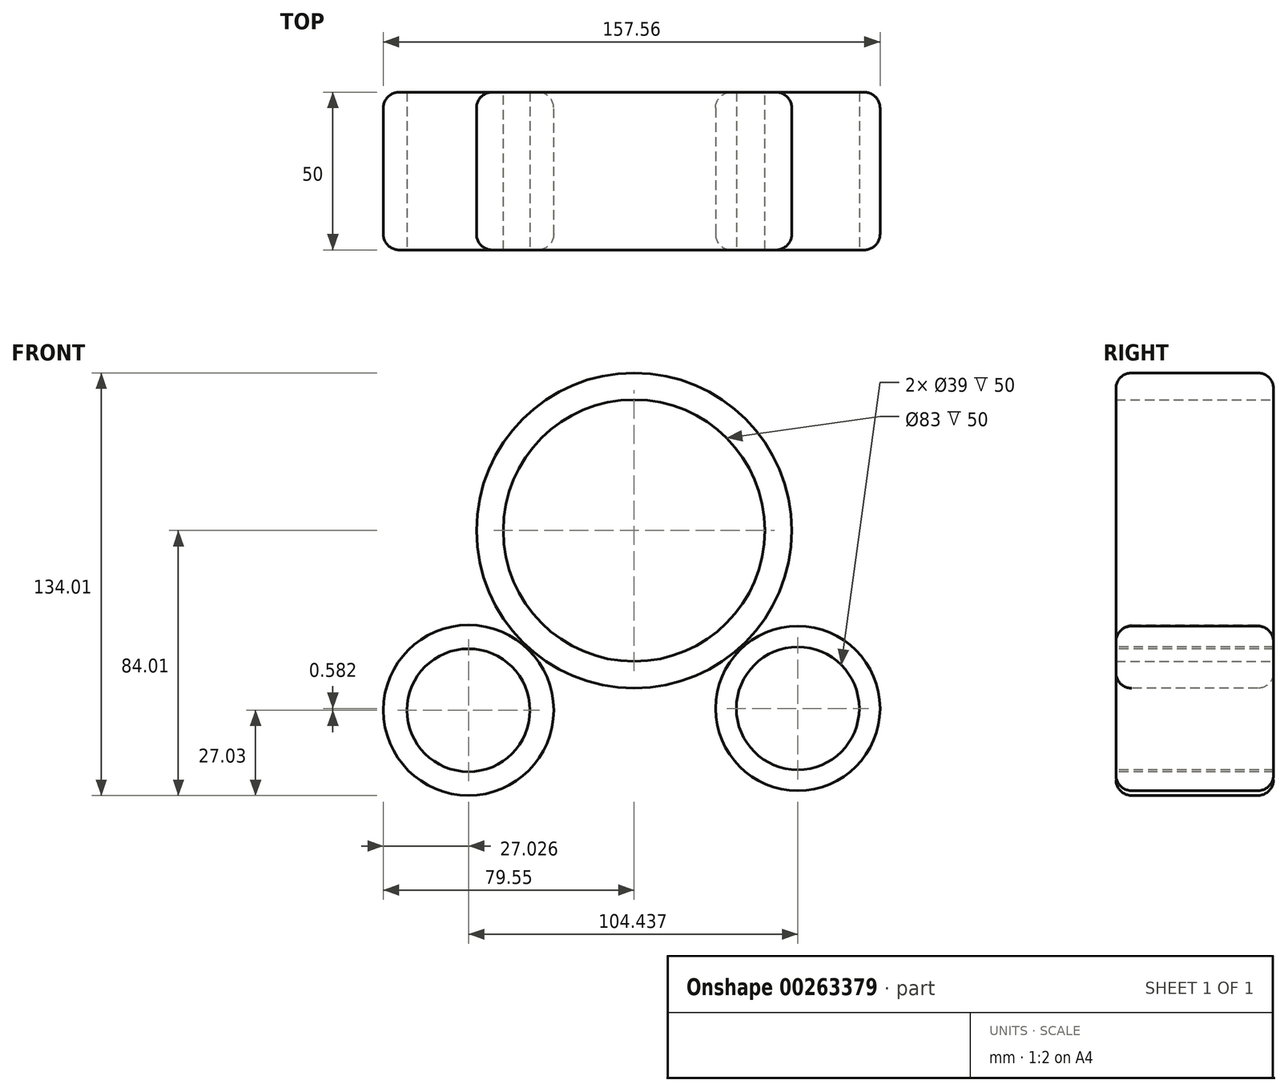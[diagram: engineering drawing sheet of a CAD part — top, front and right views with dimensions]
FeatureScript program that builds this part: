
annotation { "Feature Type Name" : "Feature", "Feature Type Description" : "" }
export const myFeature = defineFeature(function(context is Context, id is Id, definition is map)
    precondition{}
    {
        {
            var Q0;
            Q0=qCreatedBy(makeId("Front.planeOp"),FACE);
            var sketch = newSketch(context, id + "F0", { "sketchPlane" : qUnion([Q0])});
            skCircle(sketch, "E0", {"center": v(0, 0) * mm, "radius": 50 * mm});
            skSolve(sketch);
        }
        {
            var Q0;
            Q0=makeQuery(id+"F0.imprint","IMPRINT",FACE,{"disambiguationData":[TD([[makeQuery(id+"F0.imprint","IMPRINT",EDGE,{"derivedFrom":sQuery(id+"F0.wireOp",EDGE,"E0")}),1.0]])]});
            extrude(context, id + "F1", {"entities" : qUnion([Q0]), "oppositeDirection" : true, "depth" : 25 * mm});
        }
        {
            var Q0;
            Q0=makeQuery(id+"F1.opExtrude","CAP_FACE",FACE,{"disambiguationData":[OSD([sQuery(id+"F0.wireOp",EDGE,"E0")])],"isStart":true});
            extrude(context, id + "F2", {"entities" : qUnion([Q0]), "operationType" : NewBodyOperationType.ADD, "depth" : 25 * mm});
        }
        {
            var Q0;
            Q0=makeQuery(id+"F1.opExtrude","CAP_EDGE",EDGE,{"disambiguationData":[OSD([sQuery(id+"F0.wireOp",EDGE,"E0")])],"isStart":false});
            var Q1;
            Q1=makeQuery(id+"F2.opExtrude","CAP_EDGE",EDGE,{"disambiguationData":[OSD([sQuery(id+"F0.wireOp",EDGE,"E0")])],"isStart":false});
            fillet(context, id + "F3", {"entities" : qUnion([Q0, Q1]), "radius" : 5 * mm, "tangentPropagation" : true, "allowEdgeOverflow" : false});
        }
        {
            var Q0;
            Q0=qCreatedBy(makeId("Front.planeOp"),FACE);
            var sketch = newSketch(context, id + "F4", { "sketchPlane" : qUnion([Q0])});
            skCircle(sketch, "E1", {"center": v(-51.08, -56.4) * mm, "radius": 26.1 * mm});
            skCircle(sketch, "E2", {"center": v(51.91, -56.4) * mm, "radius": 26.1 * mm});
            skSolve(sketch);
        }
        {
            var Q0;
            Q0=makeQuery(id+"F4.imprint","IMPRINT",FACE,{"disambiguationData":[TD([[makeQuery(id+"F4.imprint","IMPRINT",EDGE,{"derivedFrom":sQuery(id+"F4.wireOp",EDGE,"E2")}),1.0]])]});
            extrude(context, id + "F5", {"entities" : qUnion([Q0]), "oppositeDirection" : true, "depth" : 25 * mm});
        }
        {
            var Q0;
            Q0=makeQuery(id+"F5.opExtrude","CAP_FACE",FACE,{"disambiguationData":[OSD([sQuery(id+"F4.wireOp",EDGE,"E2")])],"isStart":true});
            extrude(context, id + "F6", {"entities" : qUnion([Q0]), "operationType" : NewBodyOperationType.ADD, "depth" : 25 * mm});
        }
        {
            var Q0;
            Q0=qCreatedBy(makeId("Front.planeOp"),FACE);
            var sketch = newSketch(context, id + "F7", { "sketchPlane" : qUnion([Q0])});
            skCircle(sketch, "E3", {"center": v(-52.52, -56.98) * mm, "radius": 27.03 * mm});
            skSolve(sketch);
        }
        {
            var Q0;
            Q0=makeQuery(id+"F7.imprint","IMPRINT",FACE,{"disambiguationData":[TD([[makeQuery(id+"F7.imprint","IMPRINT",EDGE,{"derivedFrom":sQuery(id+"F7.wireOp",EDGE,"E3")}),1.0]])]});
            extrude(context, id + "F8", {"entities" : qUnion([Q0]), "depth" : 25 * mm});
        }
        {
            var Q0;
            Q0=makeQuery(id+"F8.opExtrude","CAP_FACE",FACE,{"disambiguationData":[OSD([sQuery(id+"F7.wireOp",EDGE,"E3")])],"isStart":true});
            extrude(context, id + "F9", {"entities" : qUnion([Q0]), "operationType" : NewBodyOperationType.ADD, "depth" : 25 * mm});
        }
        {
            var Q0;
            Q0=makeQuery(id+"F6.opExtrude","CAP_EDGE",EDGE,{"disambiguationData":[OSD([sQuery(id+"F4.wireOp",EDGE,"E2")])],"isStart":false});
            var Q1;
            Q1=makeQuery(id+"F5.opExtrude","CAP_EDGE",EDGE,{"disambiguationData":[OSD([sQuery(id+"F4.wireOp",EDGE,"E2")])],"isStart":false});
            var Q2;
            Q2=makeQuery(id+"F8.opExtrude","CAP_EDGE",EDGE,{"disambiguationData":[OSD([sQuery(id+"F7.wireOp",EDGE,"E3")])],"isStart":false});
            var Q3;
            Q3=makeQuery(id+"F9.opExtrude","CAP_EDGE",EDGE,{"disambiguationData":[OSD([sQuery(id+"F7.wireOp",EDGE,"E3")])],"isStart":false});
            fillet(context, id + "F10", {"entities" : qUnion([Q0, Q1, Q2, Q3]), "radius" : 5 * mm, "tangentPropagation" : true, "allowEdgeOverflow" : false});
        }
        {
            var Q0;
            Q0=qCreatedBy(makeId("Front.planeOp"),FACE);
            var sketch = newSketch(context, id + "F11", { "sketchPlane" : qUnion([Q0])});
            skCircle(sketch, "E4", {"center": v(0, 0) * mm, "radius": 41.5 * mm});
            skSolve(sketch);
        }
        {
            var Q0;
            Q0=sQuery(id+"F11.wireOp",VERTEX,"E4.center");
            var Q1;
            Q1=makeQuery(id+"F1.opExtrude","SWEPT_BODY",BODY,{"disambiguationData":[OSD([sQuery(id+"F0.wireOp",EDGE,"E0")])]});
            hole(context, id + "F12", {"style" : HoleStyle.SIMPLE, "endStyle" : HoleEndStyle.BLIND, "oppositeDirection" : true, "holeDiameter" : 83 * mm, "holeDepth" : 125 * mm, "tappedDepth" : 12 * mm, "tapClearance" : 3, "startFromSketch" : true, "locations" : qUnion([Q0]), "scope" : qUnion([Q1])});
        }
        {
            var Q0;
            Q0=qCreatedBy(makeId("Front.planeOp"),FACE);
            var sketch = newSketch(context, id + "F13", { "sketchPlane" : qUnion([Q0])});
            skCircle(sketch, "E5", {"center": v(0, 0) * mm, "radius": 41.5 * mm});
            skSolve(sketch);
        }
        {
            var Q0;
            Q0=sQuery(id+"F13.wireOp",VERTEX,"E5.center");
            var Q1;
            Q1=makeQuery(id+"F1.opExtrude","SWEPT_BODY",BODY,{"disambiguationData":[OSD([sQuery(id+"F0.wireOp",EDGE,"E0")])]});
            hole(context, id + "F14", {"style" : HoleStyle.SIMPLE, "endStyle" : HoleEndStyle.BLIND, "holeDiameter" : 83 * mm, "holeDepth" : 125 * mm, "tappedDepth" : 12 * mm, "tapClearance" : 3, "startFromSketch" : true, "locations" : qUnion([Q0]), "scope" : qUnion([Q1])});
        }
        {
            var Q0;
            Q0=makeQuery(id+"F8.opExtrude","CAP_FACE",FACE,{"disambiguationData":[OSD([sQuery(id+"F7.wireOp",EDGE,"E3")])],"isStart":false});
            var sketch = newSketch(context, id + "F15", { "sketchPlane" : qUnion([Q0])});
            skCircle(sketch, "E6", {"center": v(-52.52, -56.98) * mm, "radius": 19.5 * mm});
            skSolve(sketch);
        }
        {
            var Q0;
            Q0=sQuery(id+"F15.wireOp",VERTEX,"E6.center");
            var Q1;
            Q1=makeQuery(id+"F8.opExtrude","SWEPT_BODY",BODY,{"disambiguationData":[OSD([sQuery(id+"F7.wireOp",EDGE,"E3")])]});
            hole(context, id + "F16", {"style" : HoleStyle.SIMPLE, "endStyle" : HoleEndStyle.BLIND, "holeDiameter" : 39 * mm, "holeDepth" : 50 * mm, "tappedDepth" : 12 * mm, "tapClearance" : 3, "startFromSketch" : true, "locations" : qUnion([Q0]), "scope" : qUnion([Q1])});
        }
        {
            var Q0;
            Q0=makeQuery(id+"F6.opExtrude","CAP_FACE",FACE,{"disambiguationData":[OSD([sQuery(id+"F4.wireOp",EDGE,"E2")])],"isStart":false});
            var sketch = newSketch(context, id + "F17", { "sketchPlane" : qUnion([Q0])});
            skCircle(sketch, "E7", {"center": v(51.91, -56.4) * mm, "radius": 19.5 * mm});
            skSolve(sketch);
        }
        {
            var Q0;
            Q0=sQuery(id+"F17.wireOp",VERTEX,"E7.center");
            var Q1;
            Q1=makeQuery(id+"F5.opExtrude","SWEPT_BODY",BODY,{"disambiguationData":[OSD([sQuery(id+"F4.wireOp",EDGE,"E2")])]});
            hole(context, id + "F18", {"style" : HoleStyle.SIMPLE, "endStyle" : HoleEndStyle.BLIND, "holeDiameter" : 39 * mm, "holeDepth" : 50 * mm, "tappedDepth" : 12 * mm, "tapClearance" : 3, "startFromSketch" : true, "locations" : qUnion([Q0]), "scope" : qUnion([Q1])});
        }
    });
